# Revit family: НЕВАТОМ_Насадка НВК, версия 1
name_source: partatom
category: Воздухораспределители
revit_build: Autodesk Revit 2017 (Build: 20170118_1100(x64)
units: mm (PartAtom-declared; Revit-internal decimal feet)

## family parameters
Всегда вертикально = Нет
На основе рабочей плоскости = Нет
Общий = Нет
При загрузке вырезать с полостями = Нет
Размер круглого соединителя = Использовать диаметр
Тип детали = Нормальный
Точка расчета площади = Нет

## types (16) — shared parameters
ADSK_Единица измерения = шт.
ADSK_Завод-изготовитель = НЕВАТОМ
ADSK_Количество = 1
ADSK_Масса_Текст = кг
ADSK_Материал наименование = Оцинкованная сталь
ADSK_Наименование = Насадок НВК
ADSK_Потеря давления воздуха = 0.0 Па
ADSK_Расход воздуха = 0.0 л/с
Nevatom_URL = https://t.me

## per-type parameters (varying)
| type | ADSK_Марка | ADSK_Размер_Высота | ADSK_Размер_Длина | ADSK_Размер_Ширина | D | D1 | Dф | H | H1 | Материал корпуса |
| 100 | Насадок  НВК-100 | 320 мм | 180 мм | 180 мм | 100 мм | 180 мм | 120 мм | 220 мм | 100 мм | Материал корпуса |
| 125 | Насадок  НВК-125 | 340 мм | 225 мм | 225 мм | 125 мм | 225 мм | 150 мм | 240 мм | 100 мм | <По категории> |
| 160 | Насадок  НВК-160 | 440 мм | 280 мм | 280 мм | 160 мм | 280 мм | 192 мм | 340 мм | 100 мм | <По категории> |
| 200 | Насадок  НВК-200 | 520 мм | 345 мм | 345 мм | 200 мм | 345 мм | 240 мм | 420 мм | 100 мм | <По категории> |
| 250 | Насадок  НВК-250 | 605 мм | 430 мм | 430 мм | 250 мм | 430 мм | 300 мм | 515 мм | 90 мм | Материал корпуса |
| 315 | Насадок  НВК-315 | 700 мм | 550 мм | 550 мм | 315 мм | 550 мм | 378 мм | 600 мм | 100 мм | <По категории> |
| 355 | Насадок  НВК-355 | 740 мм | 615 мм | 615 мм | 355 мм | 615 мм | 426 мм | 620 мм | 120 мм | <По категории> |
| 400 | Насадок  НВК-400 | 790 мм | 682 мм | 682 мм | 400 мм | 682 мм | 480 мм | 670 мм | 120 мм | <По категории> |
| 450 | Насадок  НВК-450 | 890 мм | 769 мм | 769 мм | 450 мм | 769 мм | 540 мм | 770 мм | 120 мм | <По категории> |
| 500 | Насадок  НВК-500 | 990 мм | 855 мм | 855 мм | 500 мм | 855 мм | 600 мм | 870 мм | 120 мм | <По категории> |
| 560 | Насадок  НВК-560 | 1080 мм | 955 мм | 955 мм | 560 мм | 955 мм | 672 мм | 960 мм | 120 мм | <По категории> |
| 630 | Насадок  НВК-630 | 1220 мм | 1075 мм | 1075 мм | 630 мм | 1075 мм | 756 мм | 1100 мм | 120 мм | <По категории> |
| 710 | Насадок  НВК-710 | 1310 мм | 1215 мм | 1215 мм | 710 мм | 1215 мм | 852 мм | 1190 мм | 120 мм | <По категории> |
| 800 | Насадок  НВК-800 | 1420 мм | 1360 мм | 1360 мм | 800 мм | 1360 мм | 960 мм | 1300 мм | 120 мм | <По категории> |
| 900 | Насадок НВК-900 | 1680 мм | 1480 мм | 1480 мм | 900 мм | 1480 мм | 1080 мм | 1500 мм | 180 мм | <По категории> |
| 1000 | Насадок  НВК-1000 | 1880 мм | 1600 мм | 1600 мм | 1000 мм | 1600 мм | 1200 мм | 1700 мм | 180 мм | <По категории> |
